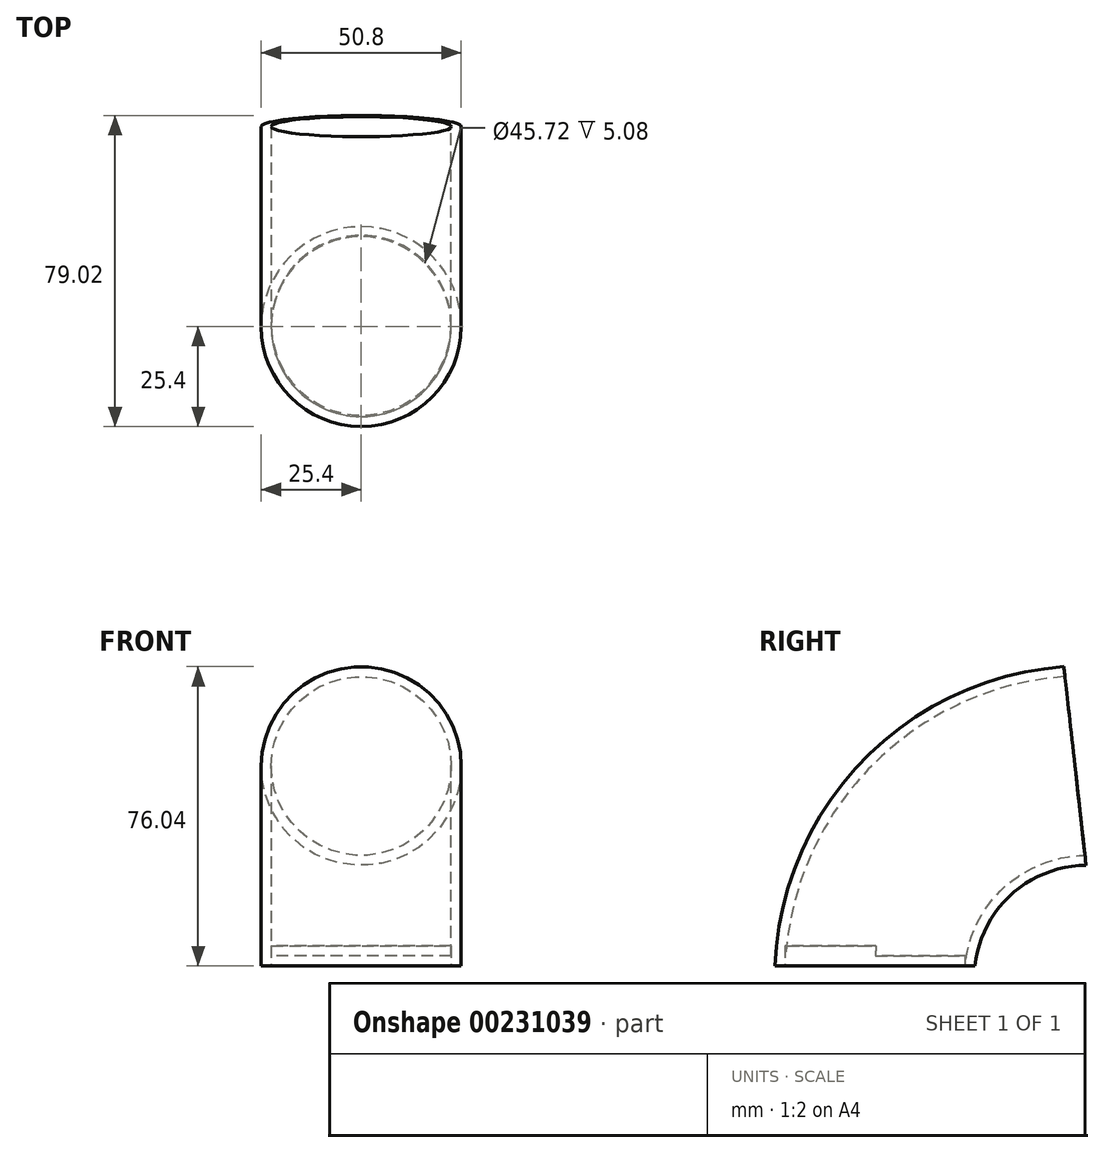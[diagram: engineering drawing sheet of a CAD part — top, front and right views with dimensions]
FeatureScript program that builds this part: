
annotation { "Feature Type Name" : "Feature", "Feature Type Description" : "" }
export const myFeature = defineFeature(function(context is Context, id is Id, definition is map)
    precondition{}
    {
        {
            var Q0;
            Q0=qCreatedBy(makeId("Top.planeOp"),FACE);
            var sketch = newSketch(context, id + "F0", { "sketchPlane" : qUnion([Q0])});
            skCircle(sketch, "E0", {"center": v(0, -50.8) * mm, "radius": 25.4 * mm});
            skSolve(sketch);
        }
        {
            var Q0;
            Q0=qCreatedBy(makeId("Right.planeOp"),FACE);
            var sketch = newSketch(context, id + "F1", { "sketchPlane" : qUnion([Q0])});
            skPoint(sketch, "E1", {"position": v(0, 50.8) * mm});
            skPoint(sketch, "E2", {"position": v(-50.8, 0) * mm});
            skArc(sketch, "E3", {"start": v(0, 50.8) * mm, "mid": v(-35.1, 35.1) * mm, "end": v(-50.8, 0) * mm});
            skSolve(sketch);
        }
        {
            var Q0;
            Q0=makeQuery(id+"F0.imprint","IMPRINT",FACE,{"disambiguationData":[TD([[makeQuery(id+"F0.imprint","IMPRINT",EDGE,{"derivedFrom":sQuery(id+"F0.wireOp",EDGE,"E0")}),1.0]])]});
            var Q1;
            Q1=sQuery(id+"F1.wireOp",EDGE,"E3");
            sweep(context, id + "F2", {"profiles" : qUnion([Q0]), "path" : qUnion([Q1])});
        }
        {
            var Q0;
            Q0=makeQuery(id+"F2.opSweep","CAP_FACE",FACE,{"disambiguationData":[OSD([sQuery(id+"F0.wireOp",EDGE,"E0"),sQuery(id+"F1.wireOp",VERTEX,"E3.start")])],"isStart":false});
            shell(context, id + "F3", {"entities" : qUnion([Q0]), "thickness" : 2.54 * mm});
        }
        {
            var Q0;
            Q0=makeQuery(id+"F2.opSweep","CAP_FACE",FACE,{"disambiguationData":[OSD([sQuery(id+"F0.wireOp",EDGE,"E0"),sQuery(id+"F1.wireOp",VERTEX,"E3.end")])],"isStart":true});
            var sketch = newSketch(context, id + "F4", { "sketchPlane" : qUnion([Q0])});
            skCircle(sketch, "E4", {"center": v(0, 50.8) * mm, "radius": 22.86 * mm});
            skSolve(sketch);
        }
        {
            var Q0;
            Q0 = qSketchRegion(id + "F4", true);
            extrude(context, id + "F5", {"entities" : qUnion([Q0]), "operationType" : NewBodyOperationType.REMOVE, "oppositeDirection" : true, "depth" : 5.08 * mm});
        }
    });
